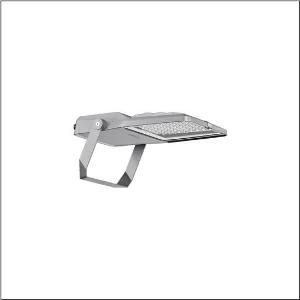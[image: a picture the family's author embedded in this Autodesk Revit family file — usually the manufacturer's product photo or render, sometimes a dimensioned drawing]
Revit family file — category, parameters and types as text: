
# Revit family: floodlight_fl_21_mini___pl43_5xa7775c2a1a_0644
name_source: partatom
category: Lighting Fixtures
units: mm (PartAtom-declared; Revit-internal decimal feet)

## family parameters
Cut with Voids When Loaded = No
Host = Face
Light Source = No
Part Type = Normal
Room Calculation Point = No
Round Connector Dimension = Use Diameter
Shared = No

## types (1)
- --- (1 x LED, 12500 lm, 89 W, 3000K)
    Apparent Load = 89 VA
    CIE Flux Codes = 27 78 99 100 100
    Color Rendering = 70
    Color Temperature = 3000K
    Default Elevation = 1800 mm
    Description = Floodlight FL 21 mini, floodlight, primary light control with lens, of PMMA, primary optical cover: protective disc, of toughened safety glass, transparent, light distribution: PL43, light emission: direct distribution, installation type: surface-mounted, LED, High Power LED, rated luminous flux: 12.500lm, luminous efficacy: 140lm/W, light colour: 730, colour temperature: 3000K, control: flexible luminous flux parameterisation, time-dependent luminous flux control, constant luminous flux control, overheat protection, presetting dimming logarithmic, with terminal, 6-pole, mains connection: 220..240V, AC, 50/60Hz, start of lifetime: 89W, end of service life: 94W, reduction: 43W, luminaire housing, of diecast aluminium, powder-coated, Siteco® metallic grey (DB 702S), corrosivity category C5 mid according to DIN EN ISO 12944, sealing non-destructively replaceable, mounting bracket, of steel, galvanised, powder-coated, Siteco® metallic grey (DB 702S), Smart Interface above, protection rating (complete): IP66, insulation class (complete): insulation class II (safety insulation), certification: CE, ENEC, VDE, protection symbol: D, impact resistance: IK08, permissible operating ambient temperature: -40..+40°C, permissible operating ambient temperature for outdoor applications: -40..+50°C, standard: DIN EN 12944, LABS conformity tested according to VDMA 24364:2018-05, packaging unit: 1 piece

Light Distribution: PL43
    Height = 70 mm
    Lamp = 1 x LED
    Lamp Light Flux = 12500 lm
    Lamp Power = 89 W
    Lamp count = 1
    Length = 485 mm
    Luminous efficacy = 140 lm/W
    Manufacturer = Siteco
    ModVariant = No
    Model = 5XA7775C2A1A
    Number of Poles = 1
    OnlyDefault = Yes
    Power Factor = 1
    Product Name = Floodlight FL 21 mini | PL43
    Product group = floodlight | pylon annexe
    ProductGroupID = 6200
    Protection Class = Protection class II
    Protection Degree = IP 66
    RLX_Detail_Level = 1
    RLX_Emergency_Light_Flux = 0 lm
    RLX_Emergency_Type = 0
    RLX_Emergency_Type_DB = No
    RlxData = <blob elided: 95713 chars, md5=92e6e9ff>
    Socket = socket
    Standby Power = 0 W
    System Light Flux = 12500 lm
    System Power = 89 W
    Type Comments = factory setting: luminous flux: 100 % | dim-lin: 254 | 456 mA
    Type Image = l_1006845.jpg
    URL = http://relux.com
    VarID = @adj_093491
    Voltage = 0 V
    Weight = 0.00 kg
    Width = 337 mm

## geometry (parser evidence)
native form markers: Blend x4, Sweep x11
no freeform markers — native parametric forms only
